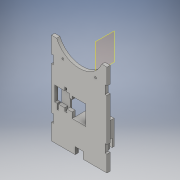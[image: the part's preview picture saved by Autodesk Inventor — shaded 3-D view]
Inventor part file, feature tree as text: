
AUTODESK INVENTOR PART (.ipt)
format: ipt  version: 2016 (Build 200138000, 138)  size: 343,040 bytes
history: native  units: in
note: dims shown in document units (in); Inventor stores cm internally (conversion verified against a paired STEP export)
features: reference x18, extrude x16, sketch x15, plane x2, projected_geometry x1
ambient origin geometry x8: Origin, YZ Plane, XZ Plane, XY Plane, X Axis, Y Axis, Z Axis, Center Point
bodies: Solid1 (feature_tree)
feature tree (52):
  extrude  "Extrusion1"  Depth=0.1969in TaperAngle=0.0deg
  extrude  "Extrusion2"  Depth=0.1969in TaperAngle=0.0deg
  extrude  "Extrusion3"  Depth=0.0787in
  extrude  "Extrusion4"  Depth=0.1969in TaperAngle=0.0deg
  extrude  "Extrusion6"  Depth=0.1969in
  extrude  "Extrusion7"  Depth=0.1969in TaperAngle=0.0deg
  extrude  "Extrusion8"  Depth=0.5in
  plane  "Work Plane1"
  extrude  "Extrusion18"  Depth=0.25in TaperAngle=0.0deg
  extrude  "Extrusion19"  Depth=0.15in
  extrude  "Extrusion21"  Depth=0.1181in
  plane  "Work Plane2"
  extrude  "Extrusion23"  Depth=1.0in TaperAngle=0.0deg
  extrude  "Extrusion24"  Depth=0.325in
  extrude  "Extrusion25"  Depth=0.0197in
  extrude  "Extrusion26"  Depth=0.0197in
  extrude  "Extrusion27"  Depth=1.0in
  extrude  "Extrusion28"  Depth=0.5in
  sketch  "Sketch1"  dims[d0=6.0in d1=0.1969in d2=0.0in]
  sketch  "Sketch2"  dims[d3=0.5906in d4=0.1969in d5=0.0in]
  reference  "Reference2"
  reference  "Reference3"
  sketch  "Sketch4"  dims[d6=3.0in d7=0.0787in]
  sketch  "Sketch6"  dims[d8=0.0787in d9=0.1969in d10=0.0in]
  sketch  "Sketch7"  dims[d11=0.1969in d12=0.1969in]
  sketch  "Sketch8"  dims[d13=0.1969in d14=0.1969in d15=0.0in]
  reference  "Reference6"
  reference  "Reference7"
  reference  "Reference8"
  reference  "Reference9"
  reference  "Reference10"
  reference  "Reference11"
  reference  "Reference12"
  reference  "Reference13"
  reference  "Reference14"
  reference  "Reference15"
  sketch  "Sketch18"  dims[d18=0.25in d19=0.5in]
  sketch  "Sketch20"  dims[d20=0.4in d21=0.0in d24=0.25in d25=0.0in]
  sketch  "Sketch22"  dims[d26=0.15in d27=0.1378in]
  sketch  "Sketch24"  dims[d28=0.0394in d29=0.1181in]
  reference  "Reference31"
  sketch  "Sketch25"  dims[d30=0.0394in d31=1.0in d32=0.0in]
  reference  "Reference32"
  reference  "Reference33"
  reference  "Reference34"
  sketch  "Sketch26"  dims[d33=0.02in d34=0.325in]
  reference  "Reference35"
  reference  "Reference36"
  sketch  "Sketch27"  dims[d35=0.02in d45=0.0197in]
  projected_geometry  "Projected Loop2"
  sketch  "Sketch28"  dims[d46=0.0197in d47=0.0197in]
  sketch  "Sketch29"  dims[d73=0.1181in d83=1.0in d84=0.5in d85=0.118in d86=1.0in d87=0.5in d88=0.118in d89=0.3937in d90=0.0in d91=0.8226in d92=0.0in d95=0.1in d96=0.0in d102=0.7in d103=1.063in d104=1.5in d106=0.7268in d107=0.8in d108=0.118in d109=0.5in d110=0.1in d111=1.2614in d112=0.0in d113=0.18in d114=0.18in d115=0.8in d116=0.3937in d117=0.0in d118=0.1181in d119=0.1181in d120=0.3937in d121=0.0in d122=0.0394in d123=0.0in d124=0.0394in d125=122.0in d126=0.0in d127=0.15in d128=122.0in d129=0.0in]
